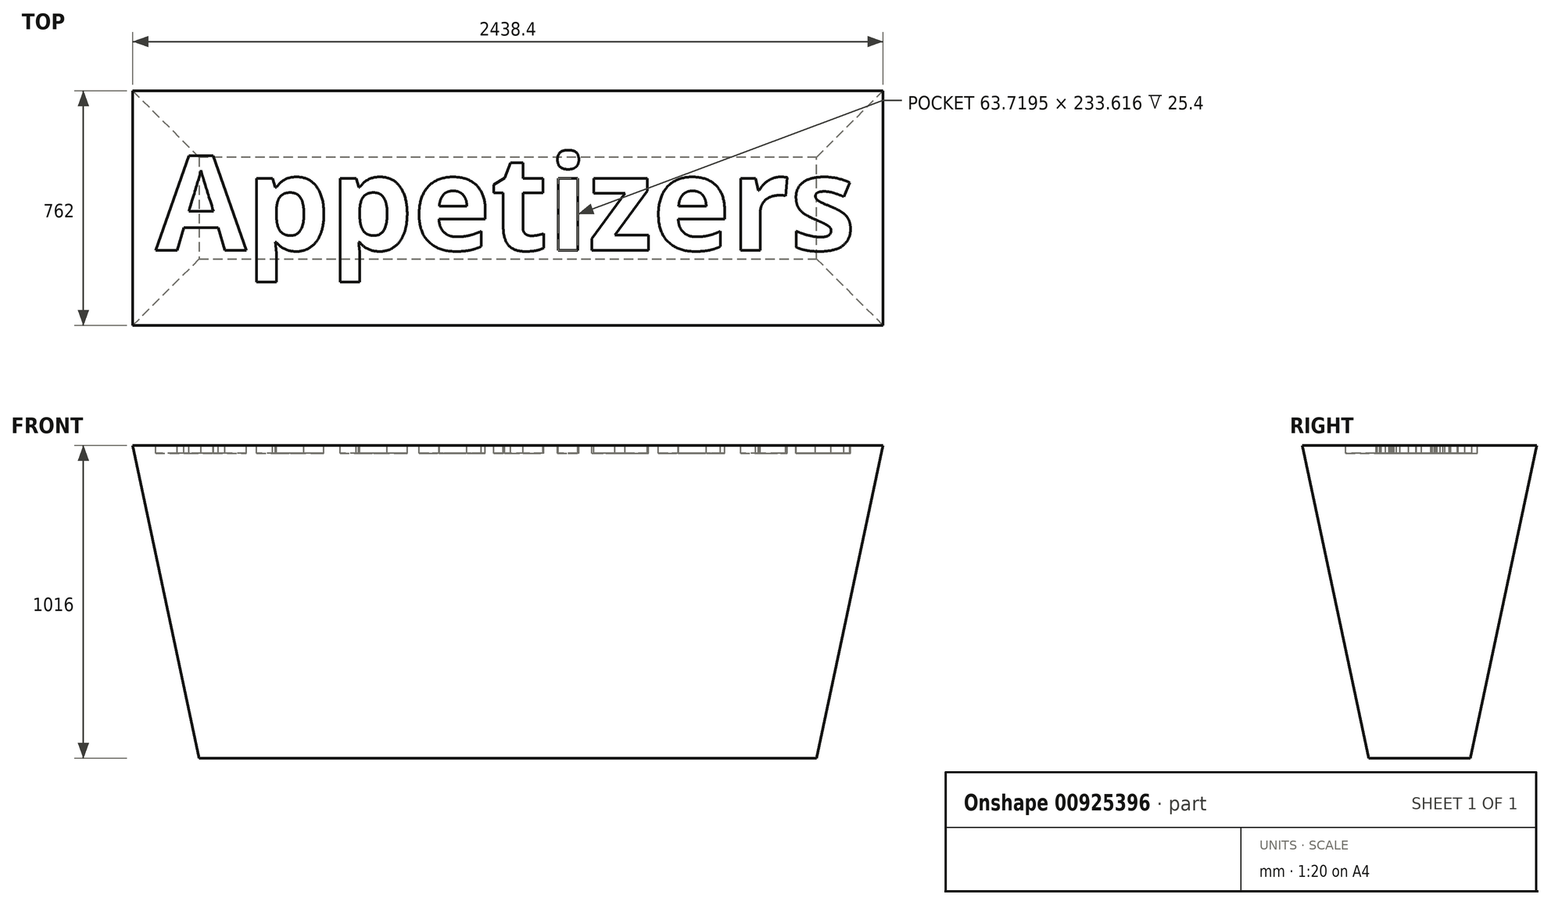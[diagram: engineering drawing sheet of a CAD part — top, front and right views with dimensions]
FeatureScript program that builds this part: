
annotation { "Feature Type Name" : "Feature", "Feature Type Description" : "" }
export const myFeature = defineFeature(function(context is Context, id is Id, definition is map)
    precondition{}
    {
        {
            var Q0;
            Q0=qCreatedBy(makeId("Top.planeOp"),FACE);
            var sketch = newSketch(context, id + "F0", { "sketchPlane" : qUnion([Q0])});
            skLineSegment(sketch, "E0.bottom", {"start": v(1219.2, -381) * mm, "end": v(-1219.2, -381) * mm});
            skLineSegment(sketch, "E0.top", {"start": v(1219.2, 381) * mm, "end": v(-1219.2, 381) * mm});
            skLineSegment(sketch, "E0.left", {"start": v(1219.2, -381) * mm, "end": v(1219.2, 381) * mm});
            skLineSegment(sketch, "E0.right", {"start": v(-1219.2, -381) * mm, "end": v(-1219.2, 381) * mm});
            skPoint(sketch, "E0.middle", {"position": v(0, 0) * mm});
            skSolve(sketch);
        }
        {
            var Q0;
            Q0=qSketchRegion(id+"F0",true);
            extrude(context, id + "F1", {"entities" : qUnion([Q0]), "oppositeDirection" : true, "depth" : 1016 * mm, "offsetDistance" : 25.4 * mm, "hasDraft" : true, "draftAngle" : 12 * degree, "draftPullDirection" : true});
        }
        {
            var Q0;
            Q0=makeQuery(id+"F1.opExtrude","CAP_FACE",FACE,{"disambiguationData":[OSD([sQuery(id+"F0.wireOp",EDGE,"E0.bottom"),sQuery(id+"F0.wireOp",EDGE,"E0.top"),sQuery(id+"F0.wireOp",EDGE,"E0.left"),sQuery(id+"F0.wireOp",EDGE,"E0.right")])],"isStart":true});
            var sketch = newSketch(context, id + "F2", { "sketchPlane" : qUnion([Q0])});
            skText(sketch, "E1", { "text": "Appetizers", "fontName": "OpenSans-Bold.ttf"});
            const initialGuessF2  = {"E1": [-1.14495, -0.13659, 1, 0, 0.3081]};
            skSetInitialGuess(sketch, initialGuessF2);
            skSolve(sketch);
        }
        {
            var Q0;
            Q0=qSketchRegion(id+"F2",true);
            extrude(context, id + "F3", {"entities" : qUnion([Q0]), "operationType" : NewBodyOperationType.REMOVE, "oppositeDirection" : true, "depth" : 25.4 * mm, "offsetDistance" : 25.4 * mm});
        }
    });
